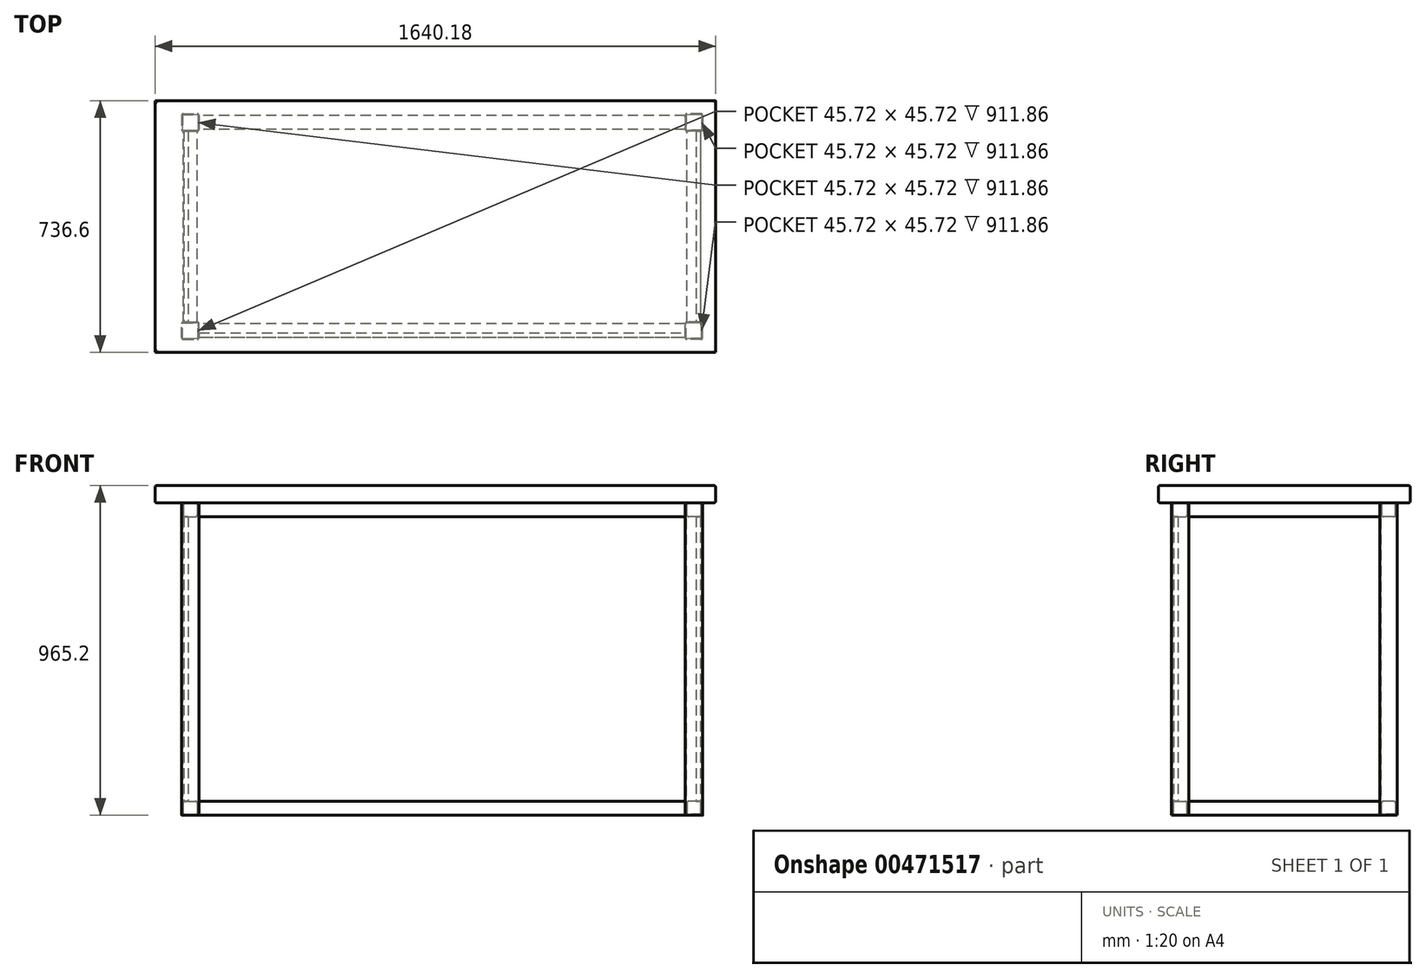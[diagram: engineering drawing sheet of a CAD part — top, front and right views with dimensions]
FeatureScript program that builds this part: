
annotation { "Feature Type Name" : "Feature", "Feature Type Description" : "" }
export const myFeature = defineFeature(function(context is Context, id is Id, definition is map)
    precondition{}
    {
        {
            var Q0;
            Q0=qCreatedBy(makeId("Top.planeOp"),FACE);
            var sketch = newSketch(context, id + "F0", { "sketchPlane" : qUnion([Q0])});
            skLineSegment(sketch, "E0.bottom", {"start": v(762, -330.2) * mm, "end": v(-762, -330.2) * mm, "construction": true});
            skLineSegment(sketch, "E0.top", {"start": v(762, 330.2) * mm, "end": v(-762, 330.2) * mm, "construction": true});
            skLineSegment(sketch, "E0.left", {"start": v(762, -330.2) * mm, "end": v(762, 330.2) * mm, "construction": true});
            skLineSegment(sketch, "E0.right", {"start": v(-762, -330.2) * mm, "end": v(-762, 330.2) * mm, "construction": true});
            skPoint(sketch, "E0.middle", {"position": v(0, 0) * mm});
            skLineSegment(sketch, "E1.bottom", {"start": v(-762, 330.2) * mm, "end": v(-711.2, 330.2) * mm});
            skLineSegment(sketch, "E1.top", {"start": v(-762, 279.4) * mm, "end": v(-711.2, 279.4) * mm});
            skLineSegment(sketch, "E1.left", {"start": v(-762, 330.2) * mm, "end": v(-762, 279.4) * mm});
            skLineSegment(sketch, "E1.right", {"start": v(-711.2, 330.2) * mm, "end": v(-711.2, 279.4) * mm});
            skSolve(sketch);
        }
        {
            var Q0;
            Q0 = qSketchRegion(id + "F0", true);
            extrude(context, id + "F1", {"entities" : qUnion([Q0]), "depth" : 914.4 * mm});
        }
        {
            var Q0;
            Q0=makeQuery(id+"F1.opExtrude","CAP_FACE",FACE,{"disambiguationData":[OSD([sQuery(id+"F0.wireOp",EDGE,"E1.bottom"),sQuery(id+"F0.wireOp",EDGE,"E1.top"),sQuery(id+"F0.wireOp",EDGE,"E1.left"),sQuery(id+"F0.wireOp",EDGE,"E1.right")])],"isStart":false});
            var Q1;
            Q1=makeQuery(id+"F1.opExtrude","SWEPT_BODY",BODY,{"disambiguationData":[OSD([sQuery(id+"F0.wireOp",EDGE,"E1.bottom"),sQuery(id+"F0.wireOp",EDGE,"E1.top"),sQuery(id+"F0.wireOp",EDGE,"E1.left"),sQuery(id+"F0.wireOp",EDGE,"E1.right")])]});
            shell(context, id + "F2", {"entities" : qUnion([Q0]), "parts" : qUnion([Q1]), "thickness" : 2.54 * mm});
        }
        {
            var Q0;
            Q0=makeQuery(id+"F1.opExtrude","SWEPT_EDGE",EDGE,{"disambiguationData":[OSD([sQuery(id+"F0.wireOp",EDGE,"E1.top"),sQuery(id+"F0.wireOp",EDGE,"E1.left")])]});
            var Q1;
            Q1=makeQuery(id+"F1.opExtrude","SWEPT_EDGE",EDGE,{"disambiguationData":[OSD([sQuery(id+"F0.wireOp",EDGE,"E1.bottom"),sQuery(id+"F0.wireOp",EDGE,"E1.left")])]});
            var Q2;
            Q2=makeQuery(id+"F1.opExtrude","SWEPT_EDGE",EDGE,{"disambiguationData":[OSD([sQuery(id+"F0.wireOp",EDGE,"E1.top"),sQuery(id+"F0.wireOp",EDGE,"E1.right")])]});
            var Q3;
            Q3=makeQuery(id+"F1.opExtrude","SWEPT_EDGE",EDGE,{"disambiguationData":[OSD([sQuery(id+"F0.wireOp",EDGE,"E1.bottom"),sQuery(id+"F0.wireOp",EDGE,"E1.right")])]});
            fillet(context, id + "F3", {"entities" : qUnion([Q0, Q1, Q2, Q3]), "radius" : 5.08 * mm, "tangentPropagation" : true, "allowEdgeOverflow" : false});
        }
        {
            var Q0;
            Q0=makeQuery(id+"F1.opExtrude","SWEPT_BODY",BODY,{"disambiguationData":[OSD([sQuery(id+"F0.wireOp",EDGE,"E1.bottom"),sQuery(id+"F0.wireOp",EDGE,"E1.top"),sQuery(id+"F0.wireOp",EDGE,"E1.left"),sQuery(id+"F0.wireOp",EDGE,"E1.right")])]});
            var Q1;
            Q1=qCreatedBy(makeId("Front.planeOp"),FACE);
            mirror(context, id + "F4", {"entities" : qUnion([Q0]), "mirrorPlane" : qUnion([Q1])});
        }
        {
            var Q0;
            Q0=makeQuery(id+"F1.opExtrude","SWEPT_BODY",BODY,{"disambiguationData":[OSD([sQuery(id+"F0.wireOp",EDGE,"E1.bottom"),sQuery(id+"F0.wireOp",EDGE,"E1.top"),sQuery(id+"F0.wireOp",EDGE,"E1.left"),sQuery(id+"F0.wireOp",EDGE,"E1.right")])]});
            var Q1;
            Q1=makeQuery(id+"F4.opPattern","COPY",BODY,{"derivedFrom":makeQuery(id+"F1.opExtrude","SWEPT_BODY",BODY,{"disambiguationData":[OSD([sQuery(id+"F0.wireOp",EDGE,"E1.bottom"),sQuery(id+"F0.wireOp",EDGE,"E1.top"),sQuery(id+"F0.wireOp",EDGE,"E1.left"),sQuery(id+"F0.wireOp",EDGE,"E1.right")])]}),"instanceName":"1"});
            var Q2;
            Q2=qCreatedBy(makeId("Right.planeOp"),FACE);
            mirror(context, id + "F5", {"entities" : qUnion([Q0, Q1]), "mirrorPlane" : qUnion([Q2])});
        }
        {
            var Q0;
            Q0=makeQuery(id+"F1.opExtrude","SWEPT_FACE",FACE,{"disambiguationData":[OSD([sQuery(id+"F0.wireOp",EDGE,"E1.right")])]});
            var sketch = newSketch(context, id + "F6", { "sketchPlane" : qUnion([Q0])});
            skLineSegment(sketch, "E2.bottom", {"start": v(284.48, 0) * mm, "end": v(325.12, 0) * mm});
            skLineSegment(sketch, "E2.top", {"start": v(284.48, 40.64) * mm, "end": v(325.12, 40.64) * mm});
            skLineSegment(sketch, "E2.left", {"start": v(284.48, 0) * mm, "end": v(284.48, 40.64) * mm});
            skLineSegment(sketch, "E2.right", {"start": v(325.12, 0) * mm, "end": v(325.12, 40.64) * mm});
            skSolve(sketch);
        }
        {
            var Q0;
            Q0 = qSketchRegion(id + "F6", true);
            var Q1;
            Q1=makeQuery(id+"F5.opPattern","COPY",FACE,{"derivedFrom":makeQuery(id+"F1.opExtrude","SWEPT_FACE",FACE,{"disambiguationData":[OSD([sQuery(id+"F0.wireOp",EDGE,"E1.right")])]}),"instanceName":"1"});
            extrude(context, id + "F7", {"entities" : qUnion([Q0]), "endBound" : BoundingType.UP_TO_SURFACE, "endBoundEntityFace" : qUnion([Q1]), "depth" : 25.4 * mm});
        }
        {
            var Q0;
            Q0=makeQuery(id+"F7.opExtrude","SWEPT_EDGE",EDGE,{"disambiguationData":[OSD([sQuery(id+"F0.wireOp",EDGE,"E1.bottom"),sQuery(id+"F0.wireOp",EDGE,"E1.right"),sQuery(id+"F6.wireOp",EDGE,"E2.top"),sQuery(id+"F6.wireOp",EDGE,"E2.right")])]});
            var Q1;
            Q1=makeQuery(id+"F7.opExtrude","SWEPT_EDGE",EDGE,{"disambiguationData":[OSD([sQuery(id+"F0.wireOp",EDGE,"E1.top"),sQuery(id+"F0.wireOp",EDGE,"E1.right"),sQuery(id+"F6.wireOp",EDGE,"E2.top"),sQuery(id+"F6.wireOp",EDGE,"E2.left")])]});
            var Q2;
            Q2=makeQuery(id+"F7.opExtrude","SWEPT_EDGE",EDGE,{"disambiguationData":[OSD([sQuery(id+"F6.wireOp",EDGE,"E2.bottom"),sQuery(id+"F6.wireOp",EDGE,"E2.right")])]});
            var Q3;
            Q3=makeQuery(id+"F7.opExtrude","SWEPT_EDGE",EDGE,{"disambiguationData":[OSD([sQuery(id+"F6.wireOp",EDGE,"E2.bottom"),sQuery(id+"F6.wireOp",EDGE,"E2.left")])]});
            fillet(context, id + "F8", {"entities" : qUnion([Q0, Q1, Q2, Q3]), "radius" : 5.08 * mm, "tangentPropagation" : true, "allowEdgeOverflow" : false});
        }
        {
            var Q0;
            Q0=makeQuery(id+"F5.opPattern","COPY",FACE,{"derivedFrom":makeQuery(id+"F1.opExtrude","CAP_FACE",FACE,{"disambiguationData":[OSD([sQuery(id+"F0.wireOp",EDGE,"E1.bottom"),sQuery(id+"F0.wireOp",EDGE,"E1.top"),sQuery(id+"F0.wireOp",EDGE,"E1.left"),sQuery(id+"F0.wireOp",EDGE,"E1.right")])],"isStart":false}),"instanceName":"1"});
            var Q1;
            Q1=makeQuery(id+"F5.opPattern","COPY",FACE,{"derivedFrom":makeQuery(id+"F1.opExtrude","CAP_FACE",FACE,{"disambiguationData":[OSD([sQuery(id+"F0.wireOp",EDGE,"E1.bottom"),sQuery(id+"F0.wireOp",EDGE,"E1.top"),sQuery(id+"F0.wireOp",EDGE,"E1.left"),sQuery(id+"F0.wireOp",EDGE,"E1.right")])],"isStart":true}),"instanceName":"1"});
            cPlane(context, id + "F9", {"entities" : qUnion([Q0, Q1]), "cplaneType" : CPlaneType.MID_PLANE, "offset" : 25.4 * mm, "width" : 152.4 * mm, "height" : 152.4 * mm});
        }
        {
            var Q0;
            Q0=makeQuery(id+"F7.opExtrude","SWEPT_BODY",BODY,{"disambiguationData":[OSD([sQuery(id+"F6.wireOp",EDGE,"E2.bottom"),sQuery(id+"F6.wireOp",EDGE,"E2.top"),sQuery(id+"F6.wireOp",EDGE,"E2.left"),sQuery(id+"F6.wireOp",EDGE,"E2.right")])]});
            var Q1;
            Q1=qCreatedBy(id+"F9.planeOp",FACE);
            mirror(context, id + "F10", {"entities" : qUnion([Q0]), "mirrorPlane" : qUnion([Q1])});
        }
        {
            var Q0;
            Q0=makeQuery(id+"F10.opPattern","COPY",BODY,{"derivedFrom":makeQuery(id+"F7.opExtrude","SWEPT_BODY",BODY,{"disambiguationData":[OSD([sQuery(id+"F6.wireOp",EDGE,"E2.bottom"),sQuery(id+"F6.wireOp",EDGE,"E2.top"),sQuery(id+"F6.wireOp",EDGE,"E2.left"),sQuery(id+"F6.wireOp",EDGE,"E2.right")])]}),"instanceName":"1"});
            var Q1;
            Q1=makeQuery(id+"F7.opExtrude","SWEPT_BODY",BODY,{"disambiguationData":[OSD([sQuery(id+"F6.wireOp",EDGE,"E2.bottom"),sQuery(id+"F6.wireOp",EDGE,"E2.top"),sQuery(id+"F6.wireOp",EDGE,"E2.left"),sQuery(id+"F6.wireOp",EDGE,"E2.right")])]});
            var Q2;
            Q2=qCreatedBy(makeId("Front.planeOp"),FACE);
            mirror(context, id + "F11", {"entities" : qUnion([Q0, Q1]), "mirrorPlane" : qUnion([Q2])});
        }
        {
            var Q0;
            Q0=makeQuery(id+"F1.opExtrude","SWEPT_FACE",FACE,{"disambiguationData":[OSD([sQuery(id+"F0.wireOp",EDGE,"E1.top")])]});
            var sketch = newSketch(context, id + "F12", { "sketchPlane" : qUnion([Q0])});
            skLineSegment(sketch, "E3.bottom", {"start": v(-756.92, 914.4) * mm, "end": v(-716.28, 914.4) * mm});
            skLineSegment(sketch, "E3.top", {"start": v(-756.92, 873.76) * mm, "end": v(-716.28, 873.76) * mm});
            skLineSegment(sketch, "E3.left", {"start": v(-756.92, 914.4) * mm, "end": v(-756.92, 873.76) * mm});
            skLineSegment(sketch, "E3.right", {"start": v(-716.28, 914.4) * mm, "end": v(-716.28, 873.76) * mm});
            skSolve(sketch);
        }
        {
            var Q0;
            Q0 = qSketchRegion(id + "F12", true);
            var Q1;
            Q1=makeQuery(id+"F4.opPattern","COPY",FACE,{"derivedFrom":makeQuery(id+"F1.opExtrude","SWEPT_FACE",FACE,{"disambiguationData":[OSD([sQuery(id+"F0.wireOp",EDGE,"E1.top")])]}),"instanceName":"1"});
            extrude(context, id + "F13", {"entities" : qUnion([Q0]), "endBound" : BoundingType.UP_TO_SURFACE, "endBoundEntityFace" : qUnion([Q1]), "depth" : 25.4 * mm});
        }
        {
            var Q0;
            Q0=makeQuery(id+"F13.opExtrude","SWEPT_EDGE",EDGE,{"disambiguationData":[OSD([sQuery(id+"F12.wireOp",EDGE,"E3.bottom"),sQuery(id+"F12.wireOp",EDGE,"E3.left")])]});
            var Q1;
            Q1=makeQuery(id+"F13.opExtrude","SWEPT_EDGE",EDGE,{"disambiguationData":[OSD([sQuery(id+"F0.wireOp",EDGE,"E1.top"),sQuery(id+"F0.wireOp",EDGE,"E1.left"),sQuery(id+"F12.wireOp",EDGE,"E3.top"),sQuery(id+"F12.wireOp",EDGE,"E3.left")])]});
            var Q2;
            Q2=makeQuery(id+"F13.opExtrude","SWEPT_EDGE",EDGE,{"disambiguationData":[OSD([sQuery(id+"F12.wireOp",EDGE,"E3.bottom"),sQuery(id+"F12.wireOp",EDGE,"E3.right")])]});
            var Q3;
            Q3=makeQuery(id+"F13.opExtrude","SWEPT_EDGE",EDGE,{"disambiguationData":[OSD([sQuery(id+"F0.wireOp",EDGE,"E1.top"),sQuery(id+"F0.wireOp",EDGE,"E1.right"),sQuery(id+"F12.wireOp",EDGE,"E3.top"),sQuery(id+"F12.wireOp",EDGE,"E3.right")])]});
            fillet(context, id + "F14", {"entities" : qUnion([Q0, Q1, Q2, Q3]), "radius" : 5.08 * mm, "tangentPropagation" : true, "allowEdgeOverflow" : false});
        }
        {
            var Q0;
            Q0=makeQuery(id+"F13.opExtrude","SWEPT_BODY",BODY,{"disambiguationData":[OSD([sQuery(id+"F12.wireOp",EDGE,"E3.bottom"),sQuery(id+"F12.wireOp",EDGE,"E3.top"),sQuery(id+"F12.wireOp",EDGE,"E3.left"),sQuery(id+"F12.wireOp",EDGE,"E3.right")])]});
            var Q1;
            Q1=qCreatedBy(id+"F9.planeOp",FACE);
            mirror(context, id + "F15", {"entities" : qUnion([Q0]), "mirrorPlane" : qUnion([Q1])});
        }
        {
            var Q0;
            Q0=makeQuery(id+"F13.opExtrude","SWEPT_BODY",BODY,{"disambiguationData":[OSD([sQuery(id+"F12.wireOp",EDGE,"E3.bottom"),sQuery(id+"F12.wireOp",EDGE,"E3.top"),sQuery(id+"F12.wireOp",EDGE,"E3.left"),sQuery(id+"F12.wireOp",EDGE,"E3.right")])]});
            var Q1;
            Q1=makeQuery(id+"F15.opPattern","COPY",BODY,{"derivedFrom":makeQuery(id+"F13.opExtrude","SWEPT_BODY",BODY,{"disambiguationData":[OSD([sQuery(id+"F12.wireOp",EDGE,"E3.bottom"),sQuery(id+"F12.wireOp",EDGE,"E3.top"),sQuery(id+"F12.wireOp",EDGE,"E3.left"),sQuery(id+"F12.wireOp",EDGE,"E3.right")])]}),"instanceName":"1"});
            var Q2;
            Q2=qCreatedBy(makeId("Right.planeOp"),FACE);
            mirror(context, id + "F16", {"entities" : qUnion([Q0, Q1]), "mirrorPlane" : qUnion([Q2])});
        }
        {
            var Q0;
            Q0=makeQuery(id+"F4.opPattern","COPY",FACE,{"derivedFrom":makeQuery(id+"F1.opExtrude","SWEPT_FACE",FACE,{"disambiguationData":[OSD([sQuery(id+"F0.wireOp",EDGE,"E1.left")])]}),"instanceName":"1"});
            cPlane(context, id + "F17", {"entities" : qUnion([Q0]), "cplaneType" : CPlaneType.OFFSET, "offset" : 6.35 * mm, "oppositeDirection" : true, "width" : 152.4 * mm, "height" : 152.4 * mm});
        }
        {
            var Q0;
            Q0=qCreatedBy(id+"F17.planeOp",FACE);
            var sketch = newSketch(context, id + "F18", { "sketchPlane" : qUnion([Q0])});
            skLineSegment(sketch, "E4.bottom", {"start": v(-279.4, 873.76) * mm, "end": v(279.4, 873.76) * mm});
            skLineSegment(sketch, "E4.top", {"start": v(-279.4, 40.64) * mm, "end": v(279.4, 40.64) * mm});
            skLineSegment(sketch, "E4.left", {"start": v(-279.4, 873.76) * mm, "end": v(-279.4, 40.64) * mm});
            skLineSegment(sketch, "E4.right", {"start": v(279.4, 873.76) * mm, "end": v(279.4, 40.64) * mm});
            skSolve(sketch);
        }
        {
            var Q0;
            Q0 = qSketchRegion(id + "F18", true);
            extrude(context, id + "F19", {"entities" : qUnion([Q0]), "oppositeDirection" : true, "depth" : 12.7 * mm});
        }
        {
            var Q0;
            Q0=makeQuery(id+"F19.opExtrude","SWEPT_BODY",BODY,{"disambiguationData":[OSD([sQuery(id+"F18.wireOp",EDGE,"E4.bottom"),sQuery(id+"F18.wireOp",EDGE,"E4.top"),sQuery(id+"F18.wireOp",EDGE,"E4.left"),sQuery(id+"F18.wireOp",EDGE,"E4.right")])]});
            var Q1;
            Q1=qCreatedBy(makeId("Right.planeOp"),FACE);
            mirror(context, id + "F20", {"entities" : qUnion([Q0]), "mirrorPlane" : qUnion([Q1])});
        }
        {
            var Q0;
            Q0=makeQuery(id+"F5.opPattern","COPY",FACE,{"derivedFrom":makeQuery(id+"F4.opPattern","COPY",FACE,{"derivedFrom":makeQuery(id+"F1.opExtrude","SWEPT_FACE",FACE,{"disambiguationData":[OSD([sQuery(id+"F0.wireOp",EDGE,"E1.bottom")])]}),"instanceName":"1"}),"instanceName":"1"});
            cPlane(context, id + "F21", {"entities" : qUnion([Q0]), "cplaneType" : CPlaneType.OFFSET, "offset" : 6.35 * mm, "oppositeDirection" : true, "width" : 152.4 * mm, "height" : 152.4 * mm});
        }
        {
            var Q0;
            Q0=qCreatedBy(id+"F21.planeOp",FACE);
            var sketch = newSketch(context, id + "F22", { "sketchPlane" : qUnion([Q0])});
            skLineSegment(sketch, "E5.bottom", {"start": v(-711.2, 873.76) * mm, "end": v(711.2, 873.76) * mm});
            skLineSegment(sketch, "E5.top", {"start": v(-711.2, 40.64) * mm, "end": v(711.2, 40.64) * mm});
            skLineSegment(sketch, "E5.left", {"start": v(-711.2, 873.76) * mm, "end": v(-711.2, 40.64) * mm});
            skLineSegment(sketch, "E5.right", {"start": v(711.2, 873.76) * mm, "end": v(711.2, 40.64) * mm});
            skSolve(sketch);
        }
        {
            var Q0;
            Q0 = qSketchRegion(id + "F22", true);
            extrude(context, id + "F23", {"entities" : qUnion([Q0]), "oppositeDirection" : true, "depth" : 12.7 * mm});
        }
        {
            var Q0;
            Q0=makeQuery(id+"F10.opPattern","COPY",FACE,{"derivedFrom":makeQuery(id+"F7.opExtrude","SWEPT_FACE",FACE,{"disambiguationData":[OSD([sQuery(id+"F6.wireOp",EDGE,"E2.bottom")])]}),"instanceName":"1"});
            var sketch = newSketch(context, id + "F24", { "sketchPlane" : qUnion([Q0])});
            skLineSegment(sketch, "E6.bottom", {"start": v(800.1, -368.3) * mm, "end": v(-840.08, -368.3) * mm});
            skLineSegment(sketch, "E6.top", {"start": v(800.1, 368.3) * mm, "end": v(-840.08, 368.3) * mm});
            skLineSegment(sketch, "E6.left", {"start": v(800.1, -368.3) * mm, "end": v(800.1, 368.3) * mm});
            skLineSegment(sketch, "E6.right", {"start": v(-840.08, -368.3) * mm, "end": v(-840.08, 368.3) * mm});
            skPoint(sketch, "E6.middle", {"position": v(-20, 0) * mm});
            skSolve(sketch);
        }
        {
            var Q0;
            Q0 = qSketchRegion(id + "F24", true);
            extrude(context, id + "F25", {"entities" : qUnion([Q0]), "depth" : 50.8 * mm});
        }
        {
            var Q0;
            Q0=makeQuery(id+"F25.opExtrude","CAP_FACE",FACE,{"disambiguationData":[OSD([sQuery(id+"F24.wireOp",EDGE,"E6.bottom"),sQuery(id+"F24.wireOp",EDGE,"E6.top"),sQuery(id+"F24.wireOp",EDGE,"E6.left"),sQuery(id+"F24.wireOp",EDGE,"E6.right")])],"isStart":false});
            var Q1;
            Q1=makeQuery(id+"F25.opExtrude","CAP_FACE",FACE,{"disambiguationData":[OSD([sQuery(id+"F24.wireOp",EDGE,"E6.bottom"),sQuery(id+"F24.wireOp",EDGE,"E6.top"),sQuery(id+"F24.wireOp",EDGE,"E6.left"),sQuery(id+"F24.wireOp",EDGE,"E6.right")])],"isStart":true});
            fillet(context, id + "F26", {"entities" : qUnion([Q0, Q1]), "radius" : 5.08 * mm, "tangentPropagation" : true, "allowEdgeOverflow" : false});
        }
    });
